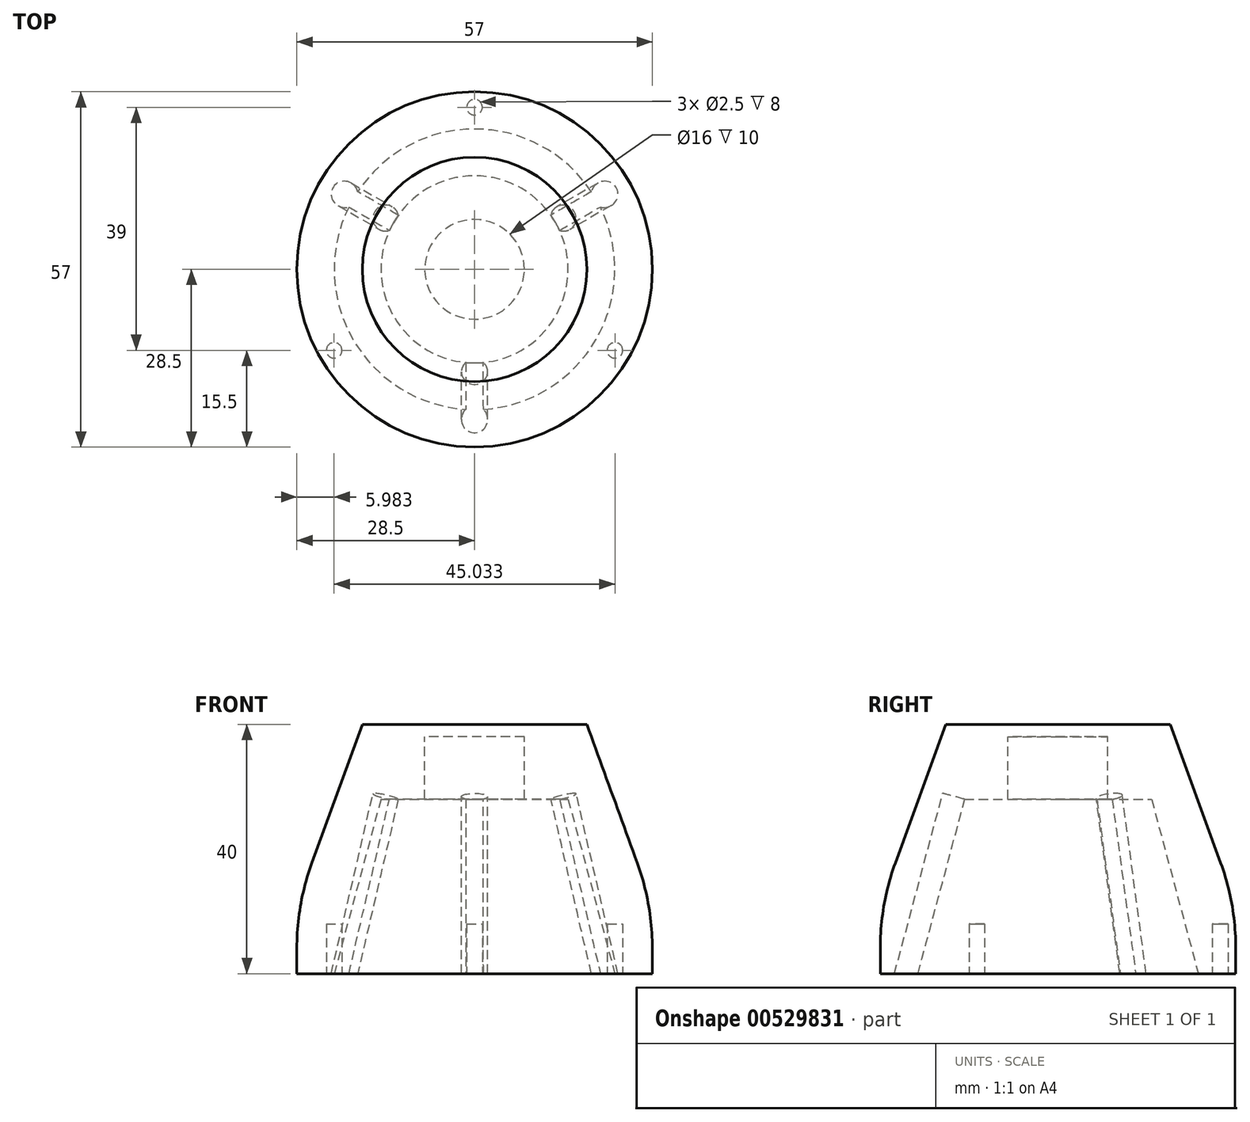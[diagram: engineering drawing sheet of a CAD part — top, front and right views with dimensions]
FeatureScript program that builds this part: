
annotation { "Feature Type Name" : "Feature", "Feature Type Description" : "" }
export const myFeature = defineFeature(function(context is Context, id is Id, definition is map)
    precondition{}
    {
        {
            var Q0;
            Q0=qCreatedBy(makeId("Front.planeOp"),FACE);
            var sketch = newSketch(context, id + "F0", { "sketchPlane" : qUnion([Q0])});
            skLineSegment(sketch, "E0", {"start": v(0, 0) * mm, "end": v(0, -2) * mm});
            skLineSegment(sketch, "E1", {"start": v(-8, -12) * mm, "end": v(-15, -12) * mm});
            skLineSegment(sketch, "E2", {"start": v(-15, -12) * mm, "end": v(-22.5, -40) * mm});
            skLineSegment(sketch, "E3", {"start": v(-22.5, -40) * mm, "end": v(-28.5, -40) * mm});
            skLineSegment(sketch, "E4", {"start": v(-28.5, -40) * mm, "end": v(-28.5, -28.85) * mm});
            skLineSegment(sketch, "E5", {"start": v(-18, 0) * mm, "end": v(0, 0) * mm});
            skLineSegment(sketch, "E6", {"start": v(-8, -12) * mm, "end": v(-8, -2) * mm});
            skLineSegment(sketch, "E7", {"start": v(-8, -2) * mm, "end": v(0, -2) * mm});
            skLineSegment(sketch, "E8", {"start": v(-28.5, -28.85) * mm, "end": v(-18, 0) * mm});
            skPoint(sketch, "E9.orphan", {"position": v(-28.5, 0) * mm});
            skSolve(sketch);
        }
        {
            var Q0;
            Q0=makeQuery(id+"F0.imprint","IMPRINT",FACE,{"disambiguationData":[TD([[makeQuery(id+"F0.imprint","IMPRINT",EDGE,{"derivedFrom":sQuery(id+"F0.wireOp",EDGE,"E0")}),-1.0]])]});
            var Q1;
            Q1=sQuery(id+"F0.wireOp",EDGE,"E0");
            revolve(context, id + "F1", {"entities" : qUnion([Q0]), "axis" : qUnion([Q1]), "revolveType" : RevolveType.FULL});
        }
        {
            var Q0;
            Q0=makeQuery(id+"F1.opRevolve","SWEPT_FACE",FACE,{"disambiguationData":[OSD([sQuery(id+"F0.wireOp",EDGE,"E1")])]});
            cPlane(context, id + "F2", {"entities" : qUnion([Q0]), "cplaneType" : CPlaneType.OFFSET, "offset" : 0 * mm, "oppositeDirection" : true, "width" : 150 * mm, "height" : 150 * mm});
        }
        {
            var Q0;
            Q0=qCreatedBy(id+"F2.planeOp",FACE);
            var sketch = newSketch(context, id + "F3", { "sketchPlane" : qUnion([Q0])});
            skCircle(sketch, "E10", {"center": v(0, 15) * mm, "radius": 2 * mm, "construction": true});
            skLineSegment(sketch, "E11", {"start": v(0, 0) * mm, "end": v(-13, -7.5) * mm, "construction": true});
            skLineSegment(sketch, "E12", {"start": v(0, 0) * mm, "end": v(13, -7.5) * mm, "construction": true});
            skCircle(sketch, "E13", {"center": v(13, -7.5) * mm, "radius": 1.83 * mm, "construction": true});
            skCircle(sketch, "E14", {"center": v(-13, -7.5) * mm, "radius": 1.8 * mm, "construction": true});
            skLineSegment(sketch, "E15", {"start": v(3.15, 15) * mm, "end": v(0, 15) * mm, "construction": true});
            skLineSegment(sketch, "E16", {"start": v(13, -7.5) * mm, "end": v(10.82, -11.26) * mm, "construction": true});
            skLineSegment(sketch, "E17", {"start": v(-13, -7.5) * mm, "end": v(-14.55, -4.8) * mm, "construction": true});
            skSolve(sketch);
        }
        {
            var Q0;
            Q0=makeQuery(id+"F1.opRevolve","SWEPT_FACE",FACE,{"disambiguationData":[OSD([sQuery(id+"F0.wireOp",EDGE,"E1")])]});
            var Q1;
            Q1=sQuery(id+"F3.wireOp",EDGE,"E15");
            cPlane(context, id + "F4", {"entities" : qUnion([Q0, Q1]), "cplaneType" : CPlaneType.LINE_ANGLE, "offset" : 25 * mm, "angle" : 15 * degree, "width" : 150 * mm, "height" : 150 * mm});
        }
        {
            var Q0;
            Q0=qCreatedBy(id+"F4.planeOp",FACE);
            var sketch = newSketch(context, id + "F5", { "sketchPlane" : qUnion([Q0])});
            skPoint(sketch, "E18.0", {"position": v(0, -11.38) * mm});
            skLineSegment(sketch, "E19", {"start": v(0, -11.38) * mm, "end": v(0, -12.88) * mm, "construction": true});
            skCircle(sketch, "E20", {"center": v(0, -12.88) * mm, "radius": 2.1 * mm});
            skSolve(sketch);
        }
        {
            var Q0;
            Q0 = qSketchRegion(id + "F5", true);
            extrude(context, id + "F6", {"entities" : qUnion([Q0]), "operationType" : NewBodyOperationType.REMOVE, "oppositeDirection" : true, "depth" : 30 * mm, "offsetDistance" : 25 * mm});
        }
        {
            var Q0;
            Q0=makeQuery(id+"F1.opRevolve","SWEPT_FACE",FACE,{"disambiguationData":[OSD([sQuery(id+"F0.wireOp",EDGE,"E1")])]});
            var Q1;
            Q1=sQuery(id+"F3.wireOp",EDGE,"E17");
            cPlane(context, id + "F7", {"entities" : qUnion([Q0, Q1]), "cplaneType" : CPlaneType.LINE_ANGLE, "offset" : 25 * mm, "angle" : 15 * degree, "oppositeDirection" : true, "width" : 150 * mm, "height" : 150 * mm});
        }
        {
            var Q0;
            Q0=qCreatedBy(id+"F7.planeOp",FACE);
            var sketch = newSketch(context, id + "F8", { "sketchPlane" : qUnion([Q0])});
            skPoint(sketch, "E21.0", {"position": v(-9.77, 5.84) * mm});
            skLineSegment(sketch, "E22", {"start": v(-9.77, 5.84) * mm, "end": v(-11.06, 6.6) * mm, "construction": true});
            skCircle(sketch, "E23", {"center": v(-11.06, 6.6) * mm, "radius": 2.1 * mm});
            skSolve(sketch);
        }
        {
            var Q0;
            Q0 = qSketchRegion(id + "F8", true);
            extrude(context, id + "F9", {"entities" : qUnion([Q0]), "operationType" : NewBodyOperationType.REMOVE, "oppositeDirection" : true, "depth" : 30 * mm, "offsetDistance" : 25 * mm});
        }
        {
            var Q0;
            Q0=makeQuery(id+"F1.opRevolve","SWEPT_FACE",FACE,{"disambiguationData":[OSD([sQuery(id+"F0.wireOp",EDGE,"E1")])]});
            var Q1;
            Q1=sQuery(id+"F3.wireOp",EDGE,"E16");
            cPlane(context, id + "F10", {"entities" : qUnion([Q0, Q1]), "cplaneType" : CPlaneType.LINE_ANGLE, "offset" : 25 * mm, "angle" : 15 * degree, "oppositeDirection" : true, "width" : 150 * mm, "height" : 150 * mm});
        }
        {
            var Q0;
            Q0=qCreatedBy(id+"F10.planeOp",FACE);
            var sketch = newSketch(context, id + "F11", { "sketchPlane" : qUnion([Q0])});
            skPoint(sketch, "E24.0", {"position": v(9.77, 5.84) * mm});
            skLineSegment(sketch, "E25", {"start": v(9.77, 5.84) * mm, "end": v(11.06, 6.6) * mm});
            skCircle(sketch, "E26", {"center": v(11.06, 6.6) * mm, "radius": 2.1 * mm});
            skSolve(sketch);
        }
        {
            var Q0;
            Q0 = qSketchRegion(id + "F11", true);
            extrude(context, id + "F12", {"entities" : qUnion([Q0]), "operationType" : NewBodyOperationType.REMOVE, "oppositeDirection" : true, "depth" : 30 * mm, "offsetDistance" : 25 * mm});
        }
        {
            var Q0;
            Q0=makeQuery(id+"F1.opRevolve","SWEPT_FACE",FACE,{"disambiguationData":[OSD([sQuery(id+"F0.wireOp",EDGE,"E3")])]});
            var sketch = newSketch(context, id + "F13", { "sketchPlane" : qUnion([Q0])});
            skCircle(sketch, "E27", {"center": v(0, -26) * mm, "radius": 1.25 * mm});
            skLineSegment(sketch, "E28", {"start": v(0, 0) * mm, "end": v(-22.52, 13) * mm, "construction": true});
            skLineSegment(sketch, "E29", {"start": v(0, 0) * mm, "end": v(22.52, 13) * mm, "construction": true});
            skCircle(sketch, "E30", {"center": v(-22.52, 13) * mm, "radius": 1.25 * mm});
            skCircle(sketch, "E31", {"center": v(22.52, 13) * mm, "radius": 1.25 * mm});
            skSolve(sketch);
        }
        {
            var Q0;
            Q0=makeQuery(id+"F13.imprint","IMPRINT",FACE,{"disambiguationData":[TD([[makeQuery(id+"F13.imprint","IMPRINT",EDGE,{"derivedFrom":sQuery(id+"F13.wireOp",EDGE,"E30")}),1.0]])]});
            var Q1;
            Q1=makeQuery(id+"F13.imprint","IMPRINT",FACE,{"disambiguationData":[TD([[makeQuery(id+"F13.imprint","IMPRINT",EDGE,{"derivedFrom":sQuery(id+"F13.wireOp",EDGE,"E31")}),1.0]])]});
            var Q2;
            Q2=makeQuery(id+"F13.imprint","IMPRINT",FACE,{"disambiguationData":[TD([[makeQuery(id+"F13.imprint","IMPRINT",EDGE,{"derivedFrom":sQuery(id+"F13.wireOp",EDGE,"E27")}),1.0]])]});
            extrude(context, id + "F14", {"entities" : qUnion([Q0, Q1, Q2]), "operationType" : NewBodyOperationType.REMOVE, "oppositeDirection" : true, "depth" : 8 * mm, "offsetDistance" : 25 * mm});
        }
        {
            var Q0;
            Q0=makeQuery(id+"F1.opRevolve","SWEPT_EDGE",EDGE,{"disambiguationData":[OSD([sQuery(id+"F0.wireOp",EDGE,"E4"),sQuery(id+"F0.wireOp",EDGE,"E8")])]});
            var Q1;
            {var subQ0=sQuery(id+"F0.wireOp",EDGE,"E8");Q1=makeQuery(id+"F17Qkg9qeZwstb8_1.opChamfer","BLEND_EDGE",EDGE,{"blendedFrom":[makeQuery(id+"F1.opRevolve","SWEPT_EDGE",EDGE,{"disambiguationData":[OSD([sQuery(id+"F0.wireOp",EDGE,"E5"),subQ0])]}),makeQuery(id+"F1.opRevolve","SWEPT_FACE",FACE,{"disambiguationData":[OSD([subQ0])]})],"blendedInto":[makeQuery(id+"F1.opRevolve","SWEPT_FACE",FACE,{"disambiguationData":[OSD([subQ0])]})]});}
            fillet(context, id + "F15", {"entities" : qUnion([Q0, Q1]), "radius" : 40 * mm, "tangentPropagation" : true, "allowEdgeOverflow" : false});
        }
    });
